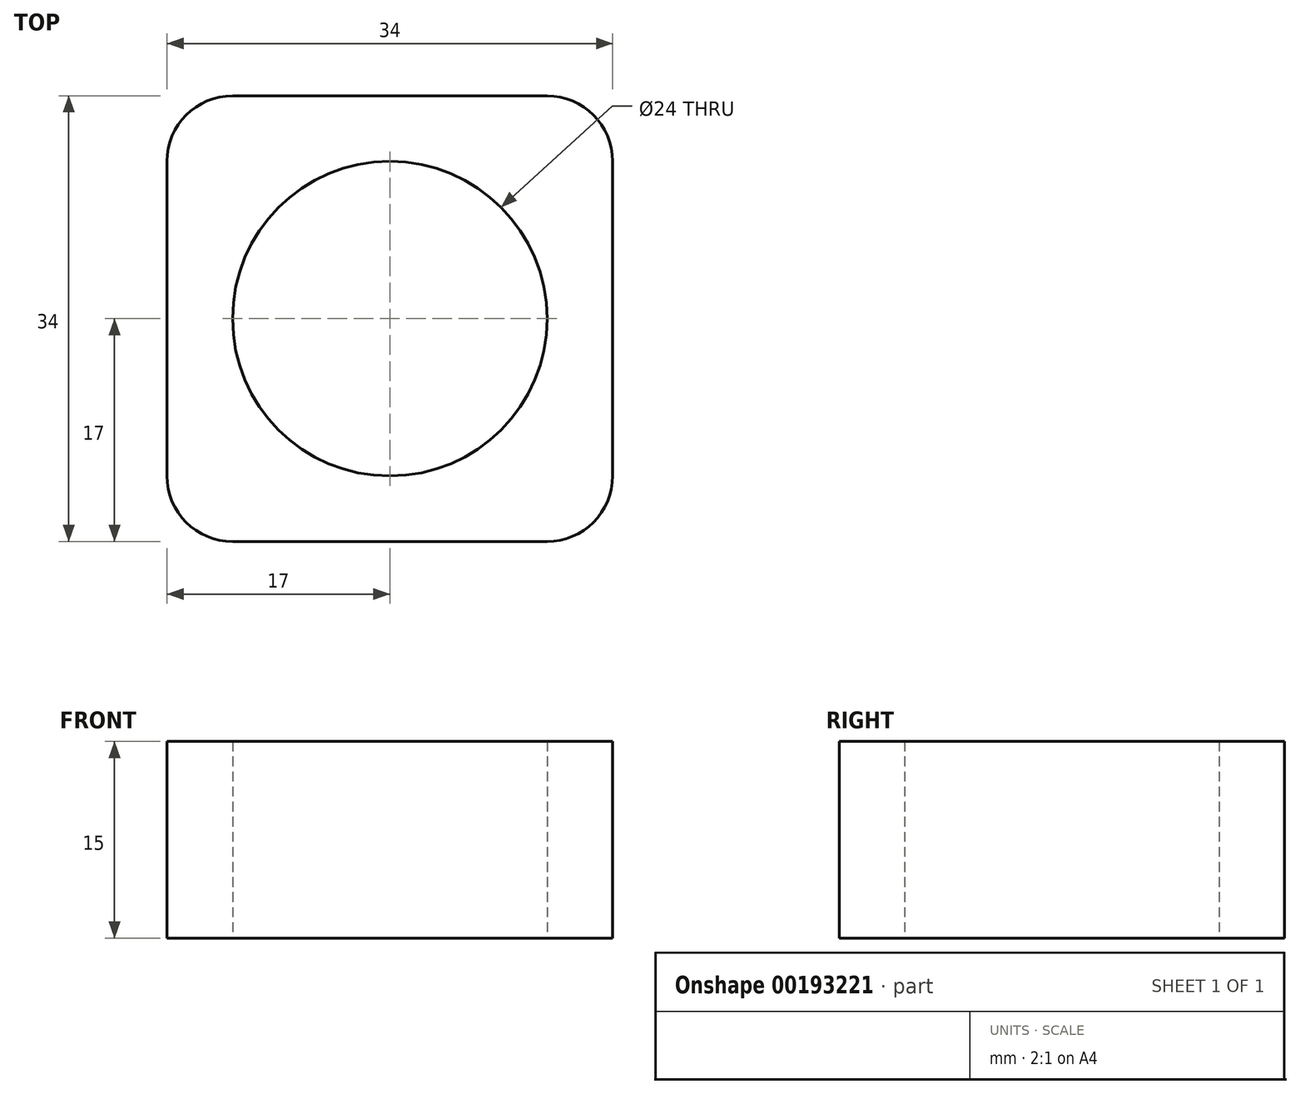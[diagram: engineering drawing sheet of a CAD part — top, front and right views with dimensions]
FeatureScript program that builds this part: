
annotation { "Feature Type Name" : "Feature", "Feature Type Description" : "" }
export const myFeature = defineFeature(function(context is Context, id is Id, definition is map)
    precondition{}
    {
        {
            var Q0;
            Q0=qCreatedBy(makeId("Top.planeOp"),FACE);
            var sketch = newSketch(context, id + "F0", { "sketchPlane" : qUnion([Q0])});
            skCircle(sketch, "E0", {"center": v(0, 0) * mm, "radius": 10 * mm});
            skCircle(sketch, "E1", {"center": v(0, 0) * mm, "radius": 12 * mm});
            skLineSegment(sketch, "E2.bottom", {"start": v(17, 17) * mm, "end": v(-17, 17) * mm});
            skLineSegment(sketch, "E2.top", {"start": v(17, -17) * mm, "end": v(-17, -17) * mm});
            skLineSegment(sketch, "E2.left", {"start": v(17, 17) * mm, "end": v(17, -17) * mm});
            skLineSegment(sketch, "E2.right", {"start": v(-17, 17) * mm, "end": v(-17, -17) * mm});
            skSolve(sketch);
        }
        {
            var Q0;
            Q0=makeQuery(id+"F0.imprint","IMPRINT",FACE,{"disambiguationData":[TD([[makeQuery(id+"F0.imprint","IMPRINT",EDGE,{"derivedFrom":sQuery(id+"F0.wireOp",EDGE,"E1")}),-1.0]])]});
            extrude(context, id + "F1", {"entities" : qUnion([Q0]), "depth" : 15 * mm});
        }
        {
            var Q0;
            Q0=makeQuery(id+"F1.opExtrude","SWEPT_EDGE",EDGE,{"disambiguationData":[OSD([sQuery(id+"F0.wireOp",EDGE,"E2.bottom"),sQuery(id+"F0.wireOp",EDGE,"E2.right")])]});
            var Q1;
            Q1=makeQuery(id+"F1.opExtrude","SWEPT_EDGE",EDGE,{"disambiguationData":[OSD([sQuery(id+"F0.wireOp",EDGE,"E2.bottom"),sQuery(id+"F0.wireOp",EDGE,"E2.left")])]});
            var Q2;
            Q2=makeQuery(id+"F1.opExtrude","SWEPT_EDGE",EDGE,{"disambiguationData":[OSD([sQuery(id+"F0.wireOp",EDGE,"E2.top"),sQuery(id+"F0.wireOp",EDGE,"E2.left")])]});
            var Q3;
            Q3=makeQuery(id+"F1.opExtrude","SWEPT_EDGE",EDGE,{"disambiguationData":[OSD([sQuery(id+"F0.wireOp",EDGE,"E2.top"),sQuery(id+"F0.wireOp",EDGE,"E2.right")])]});
            fillet(context, id + "F2", {"entities" : qUnion([Q0, Q1, Q2, Q3]), "radius" : 5 * mm, "tangentPropagation" : true, "allowEdgeOverflow" : false});
        }
    });
